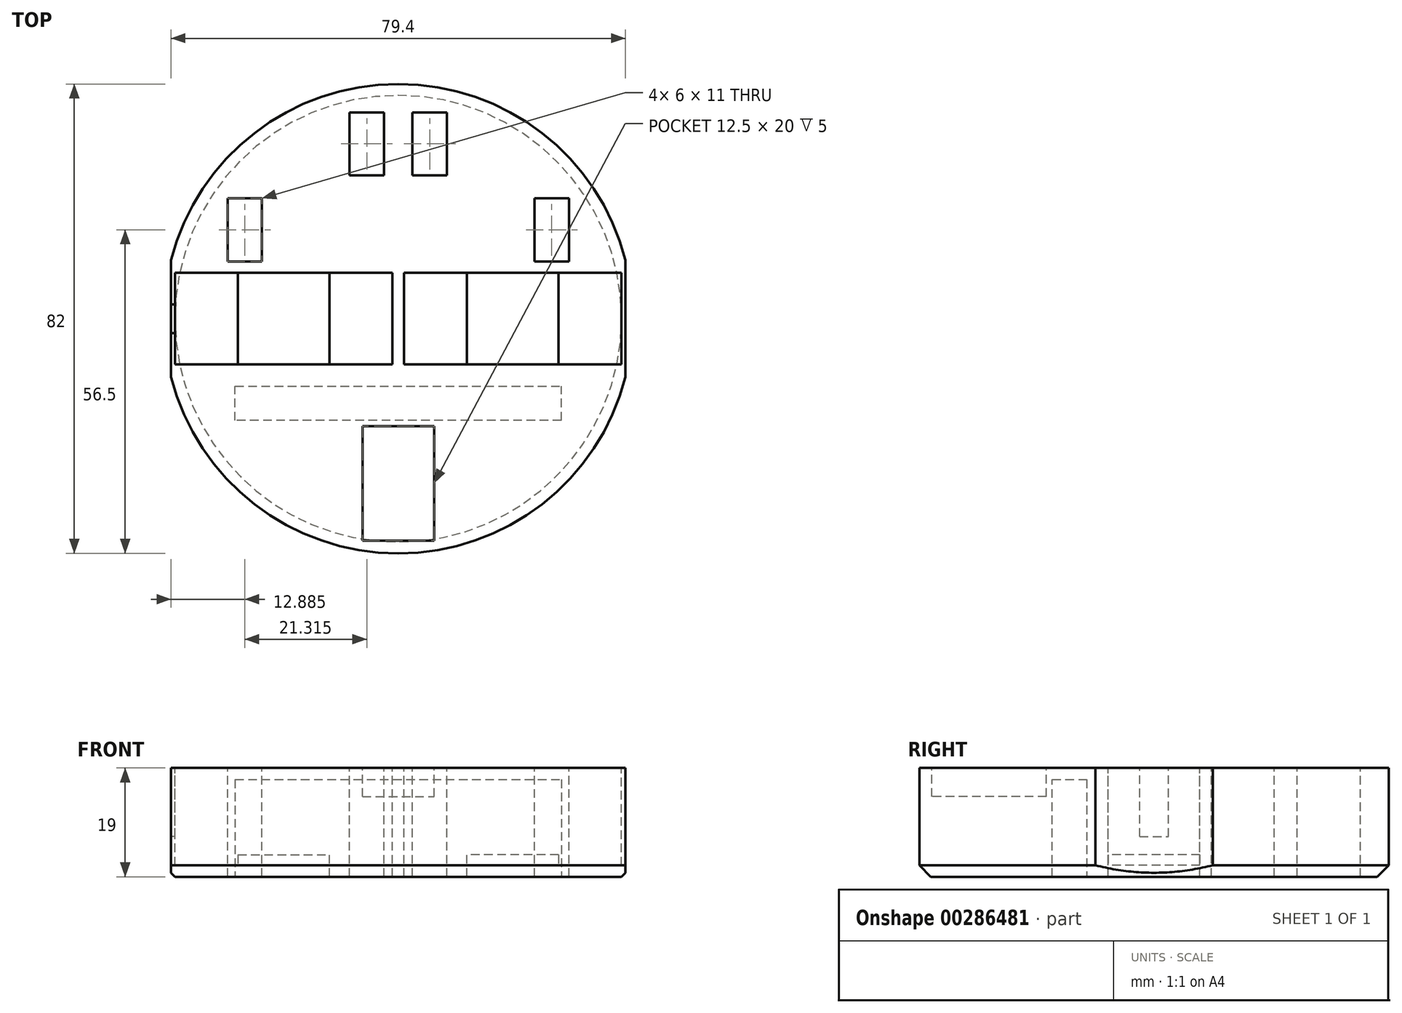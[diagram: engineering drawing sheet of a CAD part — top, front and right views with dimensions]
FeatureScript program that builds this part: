
annotation { "Feature Type Name" : "Feature", "Feature Type Description" : "" }
export const myFeature = defineFeature(function(context is Context, id is Id, definition is map)
    precondition{}
    {
        {
            var Q0;
            Q0=qCreatedBy(makeId("Top.planeOp"),FACE);
            var sketch = newSketch(context, id + "F0", { "sketchPlane" : qUnion([Q0])});
            skCircle(sketch, "E0", {"center": v(0, 0) * mm, "radius": 41 * mm});
            skSolve(sketch);
        }
        {
            var Q0;
            Q0=qSketchRegion(id+"F0",true);
            extrude(context, id + "F1", {"entities" : qUnion([Q0]), "depth" : 19 * mm, "offsetDistance" : 25 * mm});
        }
        {
            var Q0;
            Q0=makeQuery(id+"F1.opExtrude","CAP_FACE",FACE,{"disambiguationData":[OSD([sQuery(id+"F0.wireOp",EDGE,"E0")])],"isStart":false});
            var sketch = newSketch(context, id + "F2", { "sketchPlane" : qUnion([Q0])});
            skLineSegment(sketch, "E1.bottom", {"start": v(39, 8) * mm, "end": v(1, 8) * mm});
            skLineSegment(sketch, "E1.top", {"start": v(39, -8) * mm, "end": v(1, -8) * mm});
            skLineSegment(sketch, "E1.left", {"start": v(39, 8) * mm, "end": v(39, -8) * mm});
            skLineSegment(sketch, "E1.right", {"start": v(1, 8) * mm, "end": v(1, -8) * mm});
            skPoint(sketch, "E1.middle", {"position": v(20, 0) * mm});
            skLineSegment(sketch, "E2.bottom", {"start": v(39, 2.5) * mm, "end": v(43, 2.5) * mm});
            skLineSegment(sketch, "E2.top", {"start": v(39, -2.5) * mm, "end": v(43, -2.5) * mm});
            skLineSegment(sketch, "E2.left", {"start": v(39, 2.5) * mm, "end": v(39, -2.5) * mm});
            skLineSegment(sketch, "E2.right", {"start": v(43, 2.5) * mm, "end": v(43, -2.5) * mm});
            skPoint(sketch, "E2.middle", {"position": v(41, 0) * mm});
            skLineSegment(sketch, "E3.bottom", {"start": v(29.5, 26) * mm, "end": v(-29.5, 26) * mm});
            skLineSegment(sketch, "E3.top", {"start": v(29.5, 10) * mm, "end": v(-29.5, 10) * mm});
            skLineSegment(sketch, "E3.left", {"start": v(29.5, 26) * mm, "end": v(29.5, 10) * mm});
            skLineSegment(sketch, "E3.right", {"start": v(-29.5, 26) * mm, "end": v(-29.5, 10) * mm});
            skPoint(sketch, "E3.middle", {"position": v(0, 18) * mm});
            skLineSegment(sketch, "E4.MirrorCS", {"start": v(29.5, -10) * mm, "end": v(-29.5, -10) * mm});
            skLineSegment(sketch, "E5.MirrorCS", {"start": v(29.5, -26) * mm, "end": v(29.5, -10) * mm});
            skLineSegment(sketch, "E6.MirrorCS", {"start": v(29.5, -26) * mm, "end": v(-29.5, -26) * mm});
            skLineSegment(sketch, "E7.MirrorCS", {"start": v(-29.5, -26) * mm, "end": v(-29.5, -10) * mm});
            skLineSegment(sketch, "E8.MirrorCS", {"start": v(-39, 8) * mm, "end": v(-1, 8) * mm});
            skLineSegment(sketch, "E9.MirrorCS", {"start": v(-1, 8) * mm, "end": v(-1, -8) * mm});
            skLineSegment(sketch, "E10.MirrorCS", {"start": v(-39, -8) * mm, "end": v(-1, -8) * mm});
            skLineSegment(sketch, "E11.MirrorCS", {"start": v(-39, -2.5) * mm, "end": v(-43, -2.5) * mm});
            skLineSegment(sketch, "E12.MirrorCS", {"start": v(-43, 2.5) * mm, "end": v(-43, -2.5) * mm});
            skLineSegment(sketch, "E13.MirrorCS", {"start": v(-39, 2.5) * mm, "end": v(-43, 2.5) * mm});
            skLineSegment(sketch, "E14.MirrorCS", {"start": v(-39, 8) * mm, "end": v(-39, -8) * mm});
            skCircle(sketch, "E15", {"center": v(0, 0) * mm, "radius": 41.32 * mm, "construction": true});
            skSolve(sketch);
        }
        {
            var Q0;
            {var subQ3=sQuery(id+"F2.wireOp",EDGE,"E1.bottom");Q0=makeQuery(id+"F2.imprint","IMPRINT",FACE,{"disambiguationData":[TD([[makeQuery(id+"F2.imprint","IMPRINT",EDGE,{"derivedFrom":subQ3}),1.0]])]});}
            var Q1;
            {var subQ1=sQuery(id+"F2.wireOp",EDGE,"E8.MirrorCS");Q1=makeQuery(id+"F2.imprint","IMPRINT",FACE,{"disambiguationData":[TD([[makeQuery(id+"F2.imprint","IMPRINT",EDGE,{"derivedFrom":subQ1}),-1.0]])]});}
            var Q2;
            {var subQ0=sQuery(id+"F2.wireOp",EDGE,"E2.right");Q2=makeQuery(id+"F2.imprint","IMPRINT",FACE,{"disambiguationData":[TD([[makeQuery(id+"F2.imprint","IMPRINT",EDGE,{"derivedFrom":subQ0}),-1.0]])]});}
            var Q3;
            {var subQ0=sQuery(id+"F2.wireOp",EDGE,"E12.MirrorCS");Q3=makeQuery(id+"F2.imprint","IMPRINT",FACE,{"disambiguationData":[TD([[makeQuery(id+"F2.imprint","IMPRINT",EDGE,{"derivedFrom":subQ0}),1.0]])]});}
            var Q4;
            {var subQ0=sQuery(id+"F2.wireOp",EDGE,"E2.left");Q4=makeQuery(id+"F2.imprint","IMPRINT",FACE,{"disambiguationData":[TD([[makeQuery(id+"F2.imprint","IMPRINT",EDGE,{"derivedFrom":subQ0}),1.0]])]});}
            var Q5;
            {var subQ0=sQuery(id+"F2.wireOp",EDGE,"E14.MirrorCS");var subQ1=sQuery(id+"F2.wireOp",EDGE,"E11.MirrorCS");var subQ2=makeQuery(id+"F2.imprint","INTERSECT",VERTEX,{"derivedFrom":[subQ1,subQ0]});Q5=makeQuery(id+"F2.imprint","IMPRINT",FACE,{"disambiguationData":[TD([[makeQuery(id+"F2.imprint","IMPRINT",EDGE,{"disambiguationData":[TD([[subQ2,-1.0]])],"derivedFrom":subQ1}),-1.0]])]});}
            extrude(context, id + "F3", {"entities" : qUnion([Q0, Q1, Q2, Q3, Q4, Q5]), "operationType" : NewBodyOperationType.REMOVE, "oppositeDirection" : true, "depth" : 17 * mm, "offsetDistance" : 25 * mm});
        }
        {
            var Q0;
            Q0=makeQuery(id+"F1.opExtrude","CAP_FACE",FACE,{"disambiguationData":[OSD([sQuery(id+"F0.wireOp",EDGE,"E0")])],"isStart":false});
            var sketch = newSketch(context, id + "F4", { "sketchPlane" : qUnion([Q0])});
            skLineSegment(sketch, "E16.bottom", {"start": v(-29.81, 21) * mm, "end": v(-23.81, 21) * mm});
            skLineSegment(sketch, "E16.top", {"start": v(-29.81, 10) * mm, "end": v(-23.81, 10) * mm});
            skLineSegment(sketch, "E16.left", {"start": v(-29.81, 21) * mm, "end": v(-29.81, 10) * mm});
            skLineSegment(sketch, "E16.right", {"start": v(-23.81, 21) * mm, "end": v(-23.81, 10) * mm});
            skLineSegment(sketch, "E17.MirrorCS", {"start": v(29.81, 21) * mm, "end": v(29.81, 10) * mm});
            skLineSegment(sketch, "E18.MirrorCS", {"start": v(29.81, 10) * mm, "end": v(23.81, 10) * mm});
            skLineSegment(sketch, "E19.MirrorCS", {"start": v(29.81, 21) * mm, "end": v(23.81, 21) * mm});
            skLineSegment(sketch, "E20.MirrorCS", {"start": v(23.81, 21) * mm, "end": v(23.81, 10) * mm});
            skLineSegment(sketch, "E21.bottom", {"start": v(-8.5, 36.03) * mm, "end": v(-2.5, 36.03) * mm});
            skLineSegment(sketch, "E21.top", {"start": v(-8.5, 25.03) * mm, "end": v(-2.5, 25.03) * mm});
            skLineSegment(sketch, "E21.left", {"start": v(-8.5, 36.03) * mm, "end": v(-8.5, 25.03) * mm});
            skLineSegment(sketch, "E21.right", {"start": v(-2.5, 36.03) * mm, "end": v(-2.5, 25.03) * mm});
            skLineSegment(sketch, "E22.MirrorCS", {"start": v(8.5, 36.03) * mm, "end": v(2.5, 36.03) * mm});
            skLineSegment(sketch, "E23.MirrorCS", {"start": v(8.5, 36.03) * mm, "end": v(8.5, 25.03) * mm});
            skLineSegment(sketch, "E24.MirrorCS", {"start": v(2.5, 36.03) * mm, "end": v(2.5, 25.03) * mm});
            skLineSegment(sketch, "E25.MirrorCS", {"start": v(8.5, 25.03) * mm, "end": v(2.5, 25.03) * mm});
            skLineSegment(sketch, "E26.bottom", {"start": v(-1, 8) * mm, "end": v(-12, 8) * mm});
            skLineSegment(sketch, "E26.top", {"start": v(-1, -8) * mm, "end": v(-12, -8) * mm});
            skLineSegment(sketch, "E26.left", {"start": v(-1, 8) * mm, "end": v(-1, -8) * mm});
            skLineSegment(sketch, "E26.right", {"start": v(-12, 8) * mm, "end": v(-12, -8) * mm});
            skLineSegment(sketch, "E27.MirrorCS", {"start": v(1, 8) * mm, "end": v(1, -8) * mm});
            skLineSegment(sketch, "E28.MirrorCS", {"start": v(1, -8) * mm, "end": v(12, -8) * mm});
            skLineSegment(sketch, "E29.MirrorCS", {"start": v(1, 8) * mm, "end": v(12, 8) * mm});
            skLineSegment(sketch, "E30.MirrorCS", {"start": v(12, 8) * mm, "end": v(12, -8) * mm});
            skLineSegment(sketch, "E31.bottom", {"start": v(-39.7, 22.6) * mm, "end": v(-50.48, 22.6) * mm});
            skLineSegment(sketch, "E31.top", {"start": v(-39.7, -22.6) * mm, "end": v(-50.48, -22.6) * mm});
            skLineSegment(sketch, "E31.left", {"start": v(-39.7, 22.6) * mm, "end": v(-39.7, -22.6) * mm});
            skLineSegment(sketch, "E31.right", {"start": v(-50.48, 22.6) * mm, "end": v(-50.48, -22.6) * mm});
            skPoint(sketch, "E31.middle", {"position": v(-45.1, 0) * mm});
            skLineSegment(sketch, "E32.MirrorCS", {"start": v(39.7, 22.6) * mm, "end": v(50.48, 22.6) * mm});
            skLineSegment(sketch, "E33.MirrorCS", {"start": v(50.48, 22.6) * mm, "end": v(50.48, -22.6) * mm});
            skLineSegment(sketch, "E34.MirrorCS", {"start": v(39.7, 22.6) * mm, "end": v(39.7, -22.6) * mm});
            skLineSegment(sketch, "E35.MirrorCS", {"start": v(39.7, -22.6) * mm, "end": v(50.48, -22.6) * mm});
            skSolve(sketch);
        }
        {
            var Q0;
            Q0=qSketchRegion(id+"F4",true);
            extrude(context, id + "F5", {"entities" : qUnion([Q0]), "operationType" : NewBodyOperationType.REMOVE, "endBound" : BoundingType.THROUGH_ALL, "oppositeDirection" : true, "depth" : 25 * mm, "offsetDistance" : 25 * mm});
        }
        {
            var Q0;
            Q0=makeQuery(id+"F1.opExtrude","CAP_FACE",FACE,{"disambiguationData":[OSD([sQuery(id+"F0.wireOp",EDGE,"E0")])],"isStart":false});
            var sketch = newSketch(context, id + "F6", { "sketchPlane" : qUnion([Q0])});
            skLineSegment(sketch, "E36.bottom", {"start": v(-39.7, 2.5) * mm, "end": v(-39, 2.5) * mm});
            skLineSegment(sketch, "E36.top", {"start": v(-39.7, -2.5) * mm, "end": v(-39, -2.5) * mm});
            skLineSegment(sketch, "E36.left", {"start": v(-39.7, 2.5) * mm, "end": v(-39.7, -2.5) * mm});
            skLineSegment(sketch, "E36.right", {"start": v(-39, 2.5) * mm, "end": v(-39, -2.5) * mm});
            skLineSegment(sketch, "E37.MirrorCS", {"start": v(39.7, 2.5) * mm, "end": v(39, 2.5) * mm});
            skLineSegment(sketch, "E38.MirrorCS", {"start": v(39.7, -2.5) * mm, "end": v(39, -2.5) * mm});
            skLineSegment(sketch, "E39.MirrorCS", {"start": v(39, 2.5) * mm, "end": v(39, -2.5) * mm});
            skLineSegment(sketch, "E40.MirrorCS", {"start": v(39.7, 2.5) * mm, "end": v(39.7, -2.5) * mm});
            skSolve(sketch);
        }
        {
            var Q0;
            Q0 = qSketchRegion(id + "F6", true);
            extrude(context, id + "F7", {"entities" : qUnion([Q0]), "operationType" : NewBodyOperationType.ADD, "endBound" : BoundingType.UP_TO_NEXT, "oppositeDirection" : true, "depth" : 5 * mm, "offsetDistance" : 25 * mm, "hasSecondDirection" : true, "secondDirectionBound" : BoundingType.UP_TO_NEXT, "secondDirectionOppositeDirection" : true, "secondDirectionDepth" : 25 * mm, "hasSecondDirectionOffset" : true, "secondDirectionOffsetDistance" : 5 * mm});
        }
        {
            var Q0;
            Q0=makeQuery(id+"F3.boolean.opBoolean","COPY",FACE,{"derivedFrom":makeQuery(id+"F3.opExtrude","CAP_FACE",FACE,{"disambiguationData":[OSD([sQuery(id+"F2.wireOp",EDGE,"E8.MirrorCS"),sQuery(id+"F2.wireOp",EDGE,"E9.MirrorCS"),sQuery(id+"F2.wireOp",EDGE,"E10.MirrorCS"),sQuery(id+"F2.wireOp",EDGE,"E11.MirrorCS"),sQuery(id+"F2.wireOp",EDGE,"E12.MirrorCS"),sQuery(id+"F2.wireOp",EDGE,"E13.MirrorCS"),sQuery(id+"F2.wireOp",EDGE,"E14.MirrorCS")])],"isStart":false})});
            var sketch = newSketch(context, id + "F8", { "sketchPlane" : qUnion([Q0])});
            skLineSegment(sketch, "E41.bottom", {"start": v(-28, 8) * mm, "end": v(-12, 8) * mm});
            skLineSegment(sketch, "E41.top", {"start": v(-28, -8) * mm, "end": v(-12, -8) * mm});
            skLineSegment(sketch, "E41.left", {"start": v(-28, 8) * mm, "end": v(-28, -8) * mm});
            skLineSegment(sketch, "E41.right", {"start": v(-12, 8) * mm, "end": v(-12, -8) * mm});
            skPoint(sketch, "E42", {"position": v(-25.5, -8) * mm});
            skLineSegment(sketch, "E43.MirrorCS", {"start": v(28, 8) * mm, "end": v(28, -8) * mm});
            skLineSegment(sketch, "E44.MirrorCS", {"start": v(12, 8) * mm, "end": v(12, -8) * mm});
            skLineSegment(sketch, "E45.MirrorCS", {"start": v(28, 8) * mm, "end": v(12, 8) * mm});
            skLineSegment(sketch, "E46.MirrorCS", {"start": v(28, -8) * mm, "end": v(12, -8) * mm});
            skPoint(sketch, "E47.MirrorP", {"position": v(25.5, -8) * mm});
            skSolve(sketch);
        }
        {
            var Q0;
            Q0 = qSketchRegion(id + "F8", true);
            extrude(context, id + "F9", {"entities" : qUnion([Q0]), "operationType" : NewBodyOperationType.ADD, "depth" : 1.82 * mm, "offsetDistance" : 25 * mm});
        }
        {
            var Q0;
            Q0=makeQuery(id+"F5.boolean.opBoolean","SPLIT",EDGE,{"disambiguationData":[OD(0.0)],"derivedFrom":makeQuery(id+"F1.opExtrude","CAP_EDGE",EDGE,{"disambiguationData":[OSD([sQuery(id+"F0.wireOp",EDGE,"E0")])],"isStart":true})});
            chamfer(context, id + "F10", {"entities" : qUnion([Q0]), "width" : 2 * mm, "tangentPropagation" : true});
        }
        {
            var Q0;
            Q0=makeQuery(id+"F1.opExtrude","CAP_FACE",FACE,{"disambiguationData":[OSD([sQuery(id+"F0.wireOp",EDGE,"E0")])],"isStart":false});
            var sketch = newSketch(context, id + "F11", { "sketchPlane" : qUnion([Q0])});
            skLineSegment(sketch, "E48.bottom", {"start": v(-6.25, -18.78) * mm, "end": v(6.25, -18.78) * mm});
            skLineSegment(sketch, "E48.top", {"start": v(-6.25, -38.78) * mm, "end": v(6.25, -38.78) * mm});
            skLineSegment(sketch, "E48.left", {"start": v(-6.25, -18.78) * mm, "end": v(-6.25, -38.78) * mm});
            skLineSegment(sketch, "E48.right", {"start": v(6.25, -18.78) * mm, "end": v(6.25, -38.78) * mm});
            skPoint(sketch, "E48.middle", {"position": v(0, -28.78) * mm});
            skSolve(sketch);
        }
        {
            var Q0;
            Q0 = qSketchRegion(id + "F11", true);
            extrude(context, id + "F12", {"entities" : qUnion([Q0]), "operationType" : NewBodyOperationType.REMOVE, "oppositeDirection" : true, "depth" : 5 * mm, "offsetDistance" : 25 * mm});
        }
        {
            var Q0;
            Q0=qCreatedBy(makeId("Right.planeOp"),FACE);
            var sketch = newSketch(context, id + "F13", { "sketchPlane" : qUnion([Q0])});
            skLineSegment(sketch, "E49", {"start": v(-11.78, 17) * mm, "end": v(-11.78, -18) * mm});
            skLineSegment(sketch, "E50", {"start": v(-11.78, -18) * mm, "end": v(-17.78, -18) * mm});
            skLineSegment(sketch, "E51", {"start": v(-17.78, -18) * mm, "end": v(-17.78, 17) * mm});
            skLineSegment(sketch, "E52", {"start": v(-17.78, 17) * mm, "end": v(-11.78, 17) * mm});
            skSolve(sketch);
        }
        {
            var Q0;
            Q0 = qSketchRegion(id + "F13", true);
            extrude(context, id + "F14", {"entities" : qUnion([Q0]), "operationType" : NewBodyOperationType.REMOVE, "oppositeDirection" : true, "depth" : 57 * mm, "offsetDistance" : 25 * mm, "symmetric" : true});
        }
    });
